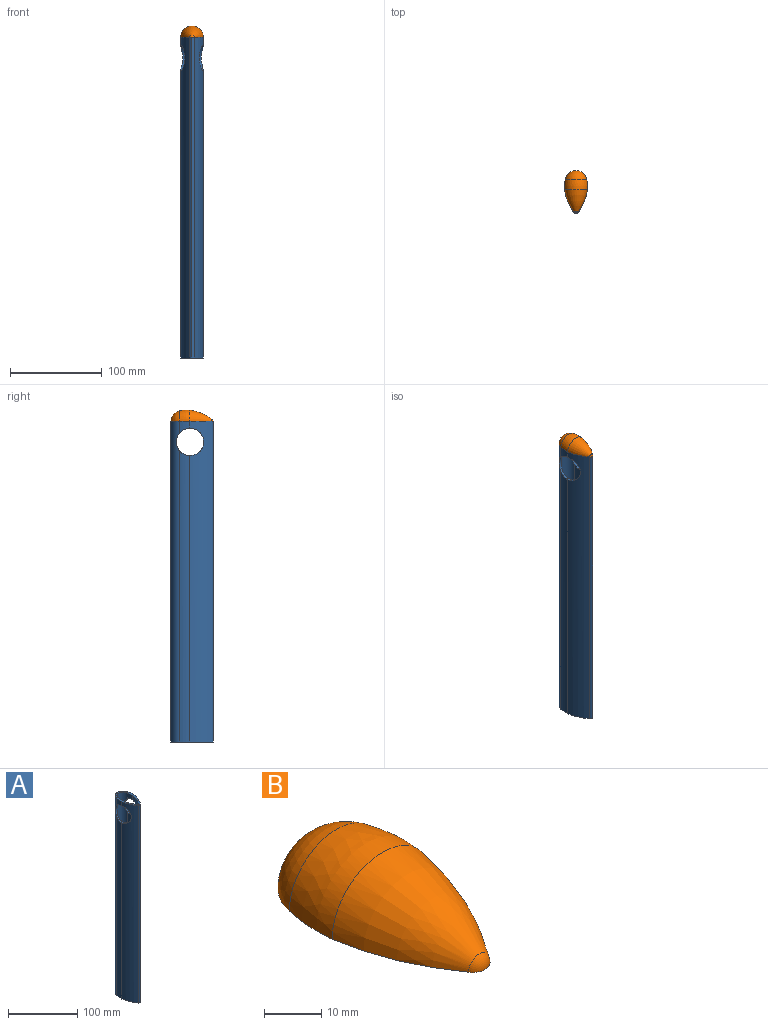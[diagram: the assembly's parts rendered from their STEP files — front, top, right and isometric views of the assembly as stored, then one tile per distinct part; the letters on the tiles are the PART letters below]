
ASSEMBLY  parts=2 mates=1
PART A: 22 faces, bbox 25x46x350 mm
  f0: cylinder r=35.8mm len=317.76mm, axis (0,0,-1), area 3566.4mm2, adj f2,f13,f19,f21
  f1: cylinder r=35.8mm len=12.53mm, axis (0,0,-1), area 101.9mm2, adj f2,f13,f18,f19
  f2: cylinder r=11.83mm len=350mm, axis (0,0,-1), area 11238.6mm2, adj f0,f1,f3,f4,f18,f19,f20,f21
  f3: cylinder r=35.8mm len=317.76mm, axis (0,0,-1), area 3566.4mm2, adj f2,f5,f20,f21
  f4: cylinder r=35.8mm len=12.53mm, axis (0,0,-1), area 101.9mm2, adj f2,f5,f18,f20
  f5: cylinder r=55.04mm len=350mm, axis (0,0,-1), area 8718.7mm2, adj f3,f4,f14,f18,f20,f21
  f6: cylinder r=52.57mm len=350mm, axis (0,0,-1), area 8324.4mm2, adj f7,f8,f17,f18,f20,f21
  f7: cylinder r=33.33mm len=317.19mm, axis (0,0,-1), area 3305.2mm2, adj f6,f9,f20,f21
  f8: cylinder r=33.33mm len=11.97mm, axis (0,0,-1), area 93.2mm2, adj f6,f9,f18,f20
  f9: cylinder r=9.36mm len=350mm, axis (0,0,-1), area 8863.5mm2, adj f7,f8,f10,f11,f18,f19,f20,f21
  f10: cylinder r=33.33mm len=317.19mm, axis (0,0,-1), area 3305.2mm2, adj f9,f12,f19,f21
  f11: cylinder r=33.33mm len=11.97mm, axis (0,0,-1), area 93.2mm2, adj f9,f12,f18,f19
  f12: cylinder r=52.57mm len=350mm, axis (0,0,-1), area 8324.4mm2, adj f10,f11,f16,f18,f19,f21
  f13: cylinder r=55.04mm len=350mm, axis (0,0,-1), area 8718.8mm2, adj f0,f1,f15,f18,f19,f21
  f14: cylinder r=2.99mm len=350mm, axis (0,0,-1), area 1084.6mm2, adj f5,f15,f18,f21
  f15: cylinder r=2.99mm len=350mm, axis (0,0,-1), area 1084.6mm2, adj f13,f14,f18,f21
  f16: cylinder r=0.52mm len=350mm, axis (0,0,-1), area 216.4mm2, adj f12,f17,f18,f21
  f17: cylinder r=0.52mm len=350mm, axis (0,0,-1), area 216.4mm2, adj f6,f16,f18,f21
  f18: plane 46x24.98mm, normal (0,0,1), area 260.6mm2, adj f1,f2,f4,f5,f6,f8,f9,f11
  f19: cylinder r=15.01mm len=30.01mm, axis (-1,0,0), area 248.4mm2, adj f0,f1,f2,f9,f10,f11,f12,f13
  f20: cylinder r=15.01mm len=30.01mm, axis (-1,0,0), area 248.6mm2, adj f2,f3,f4,f5,f6,f7,f8,f9
  f21: plane 46x24.98mm, normal (0,0,-1), area 260.6mm2, adj f0,f2,f3,f5,f6,f7,f9,f10
PART B: 9 faces, bbox 25x46x12.5 mm
  f0: torus R=0.03mm, axis (0,1,0), area 0.5mm2, adj f7,f8
  f1: torus R=0.03mm, axis (0,1,0), area 13.8mm2, adj f2,f8
  f2: revolved ~24.68x23.81mm, area 685.3mm2, adj f1,f3,f8
  f3: revolved ~24.98x12.49mm, area 437.4mm2, adj f2,f4,f8
  f4: sphere r=11.83mm, area 352mm2, adj f3,f8
  f5: sphere r=9.33mm, area 219.8mm2, adj f6,f8
  f6: revolved ~19.98x10.45mm, area 323mm2, adj f5,f7,f8
  f7: revolved ~22.77x19.71mm, area 473.6mm2, adj f0,f6,f8
  f8: plane 46x24.98mm, normal (0,0,-1), area 263.5mm2, adj f0,f1,f2,f3,f4,f5,f6,f7
PLACE A t=(11.23,-104.26,-41.11)mm
PLACE B t=(11.23,-104.26,8.89)mm
MATE fastened B.f8 <-> A.f18  axis (0,0,1) through (11.23,-127.26,8.89)mm
